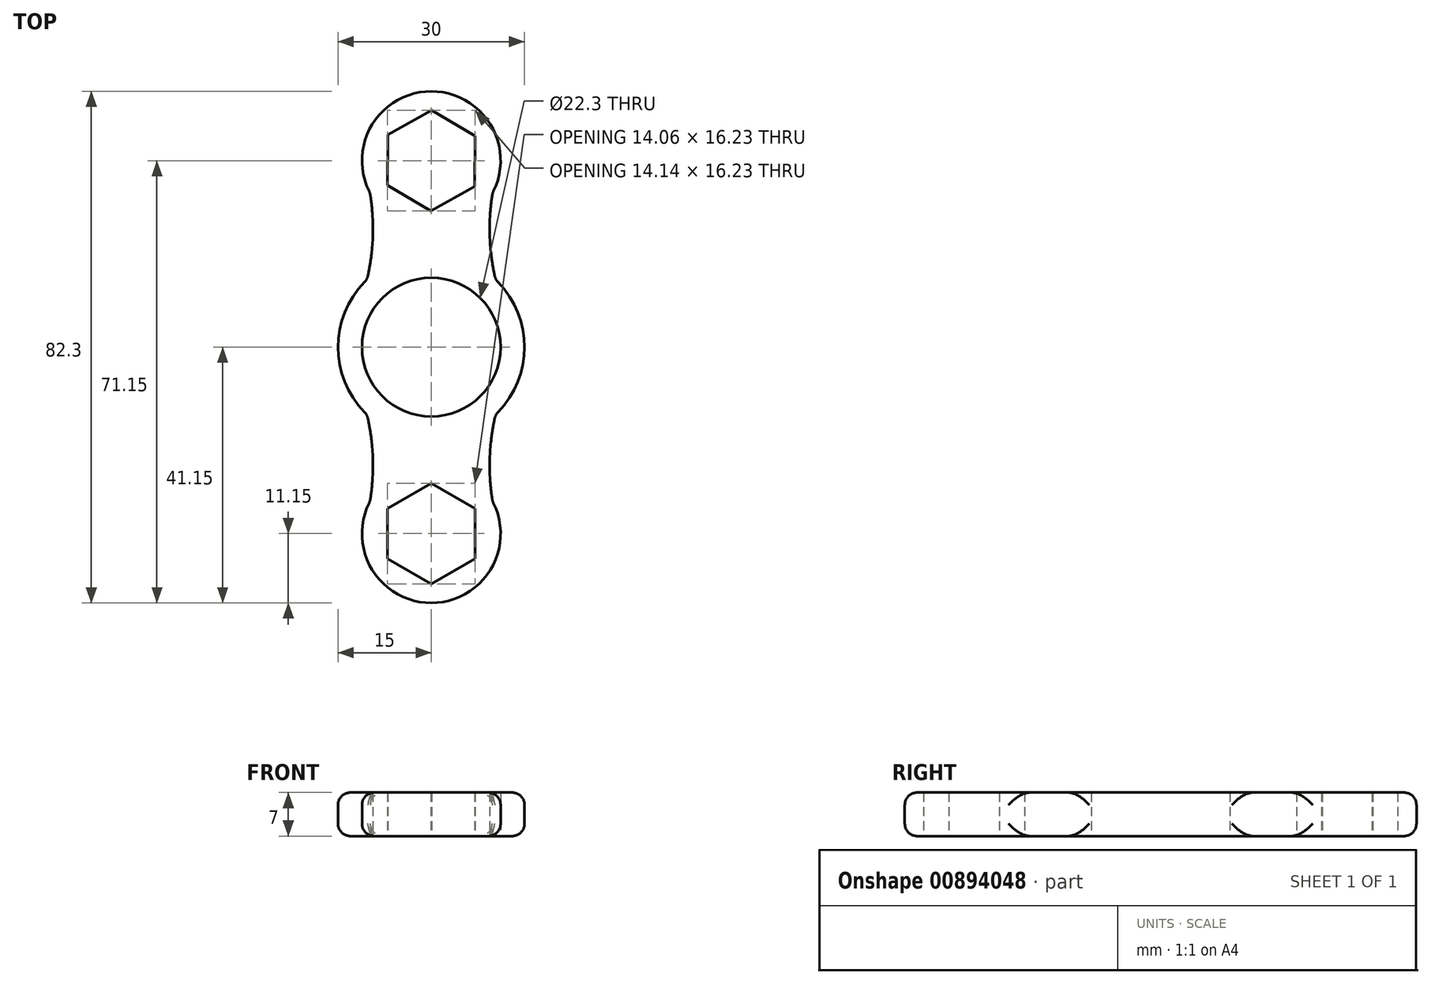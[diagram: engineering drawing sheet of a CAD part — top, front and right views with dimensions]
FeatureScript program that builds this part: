
annotation { "Feature Type Name" : "Feature", "Feature Type Description" : "" }
export const myFeature = defineFeature(function(context is Context, id is Id, definition is map)
    precondition{}
    {
        {
            var Q0;
            Q0=qCreatedBy(makeId("Top.planeOp"),FACE);
            var sketch = newSketch(context, id + "F0", { "sketchPlane" : qUnion([Q0])});
            skCircle(sketch, "E0", {"center": v(0, 0) * mm, "radius": 11.15 * mm});
            skLineSegment(sketch, "E1.0", {"start": v(6.98, 25.87) * mm, "end": v(-0.09, 21.88) * mm});
            skLineSegment(sketch, "E1.1", {"start": v(-0.09, 21.88) * mm, "end": v(-7.07, 26.02) * mm});
            skLineSegment(sketch, "E1.2", {"start": v(-7.07, 26.02) * mm, "end": v(-6.98, 34.13) * mm});
            skLineSegment(sketch, "E1.3", {"start": v(-6.98, 34.13) * mm, "end": v(0.09, 38.12) * mm});
            skLineSegment(sketch, "E1.4", {"start": v(0.09, 38.12) * mm, "end": v(7.07, 33.98) * mm});
            skLineSegment(sketch, "E1.5", {"start": v(7.07, 33.98) * mm, "end": v(6.98, 25.87) * mm});
            skPoint(sketch, "E1.0.midPoint", {"position": v(3.45, 23.88) * mm});
            skLineSegment(sketch, "E2.0", {"start": v(-7.03, -34.06) * mm, "end": v(-7.03, -25.94) * mm});
            skLineSegment(sketch, "E2.1", {"start": v(-7.03, -25.94) * mm, "end": v(0, -21.88) * mm});
            skLineSegment(sketch, "E2.2", {"start": v(0, -21.88) * mm, "end": v(7.03, -25.94) * mm});
            skLineSegment(sketch, "E2.3", {"start": v(7.03, -25.94) * mm, "end": v(7.03, -34.06) * mm});
            skLineSegment(sketch, "E2.4", {"start": v(7.03, -34.06) * mm, "end": v(0, -38.12) * mm});
            skLineSegment(sketch, "E2.5", {"start": v(0, -38.12) * mm, "end": v(-7.03, -34.06) * mm});
            skPoint(sketch, "E2.0.midPoint", {"position": v(-7.03, -30) * mm});
            skLineSegment(sketch, "E3", {"start": v(0, 0) * mm, "end": v(-11.15, 0) * mm, "construction": true});
            skCircle(sketch, "E4", {"center": v(0, 30) * mm, "radius": 11.15 * mm});
            skCircle(sketch, "E5", {"center": v(0, 0) * mm, "radius": 15 * mm});
            skCircle(sketch, "E6", {"center": v(0, -30) * mm, "radius": 11.15 * mm});
            skArc(sketch, "E7", {"start": v(-10.35, 10.86) * mm, "mid": v(-9.41, 20.49) * mm, "end": v(-11.15, 30) * mm});
            skArc(sketch, "E8", {"start": v(-11.15, -30) * mm, "mid": v(-9.41, -20.49) * mm, "end": v(-10.35, -10.86) * mm});
            skArc(sketch, "E9", {"start": v(11.15, 30) * mm, "mid": v(9.41, 20.49) * mm, "end": v(10.35, 10.86) * mm});
            skArc(sketch, "E10", {"start": v(10.35, -10.86) * mm, "mid": v(9.41, -20.49) * mm, "end": v(11.15, -30) * mm});
            skPoint(sketch, "E11.orphan", {"position": v(15, 0) * mm});
            skPoint(sketch, "E12.orphan", {"position": v(-15, 0) * mm});
            skPoint(sketch, "E13.start.orphan", {"position": v(11.15, 0) * mm});
            skLineSegment(sketch, "E14.trimOffspring", {"start": v(0, 21.93) * mm, "end": v(0, 22.97) * mm, "construction": true});
            skLineSegment(sketch, "E15.trimOffspring", {"start": v(0, -21.88) * mm, "end": v(0, -22.97) * mm, "construction": true});
            skSolve(sketch);
        }
        {
            var Q0;
            Q0 = qSketchRegion(id + "F0", true);
            extrude(context, id + "F1", {"entities" : qUnion([Q0]), "depth" : 7 * mm, "offsetDistance" : 25 * mm});
        }
        {
            var Q0;
            Q0=makeQuery(id+"F1.opExtrude","SWEPT_FACE",FACE,{"disambiguationData":[OSD([sQuery(id+"F0.wireOp",EDGE,"E4")])]});
            var Q1;
            {var subQ0=sQuery(id+"F0.wireOp",EDGE,"E5");Q1=makeQuery(id+"F1.opExtrude","SWEPT_FACE",FACE,{"disambiguationData":[OSD([subQ0]),TDD([makeQuery(id+"F0.imprint","IMPRINT",EDGE,{"disambiguationData":[TD([[makeQuery(id+"F0.imprint","INTERSECT",VERTEX,{"derivedFrom":[subQ0,sQuery(id+"F0.wireOp",EDGE,"E7")]}),-1.0]])],"derivedFrom":subQ0})])]});}
            var Q2;
            Q2=makeQuery(id+"F1.opExtrude","SWEPT_FACE",FACE,{"disambiguationData":[OSD([sQuery(id+"F0.wireOp",EDGE,"E6")])]});
            var Q3;
            {var subQ0=sQuery(id+"F0.wireOp",EDGE,"E5");Q3=makeQuery(id+"F1.opExtrude","SWEPT_FACE",FACE,{"disambiguationData":[OSD([subQ0]),TDD([makeQuery(id+"F0.imprint","IMPRINT",EDGE,{"disambiguationData":[TD([[makeQuery(id+"F0.imprint","INTERSECT",VERTEX,{"derivedFrom":[subQ0,sQuery(id+"F0.wireOp",EDGE,"E9")]}),1.0]])],"derivedFrom":subQ0})])]});}
            fillet(context, id + "F2", {"entities" : qUnion([Q0, Q1, Q2, Q3]), "radius" : 2 * mm, "tangentPropagation" : true, "allowEdgeOverflow" : false});
        }
    });
